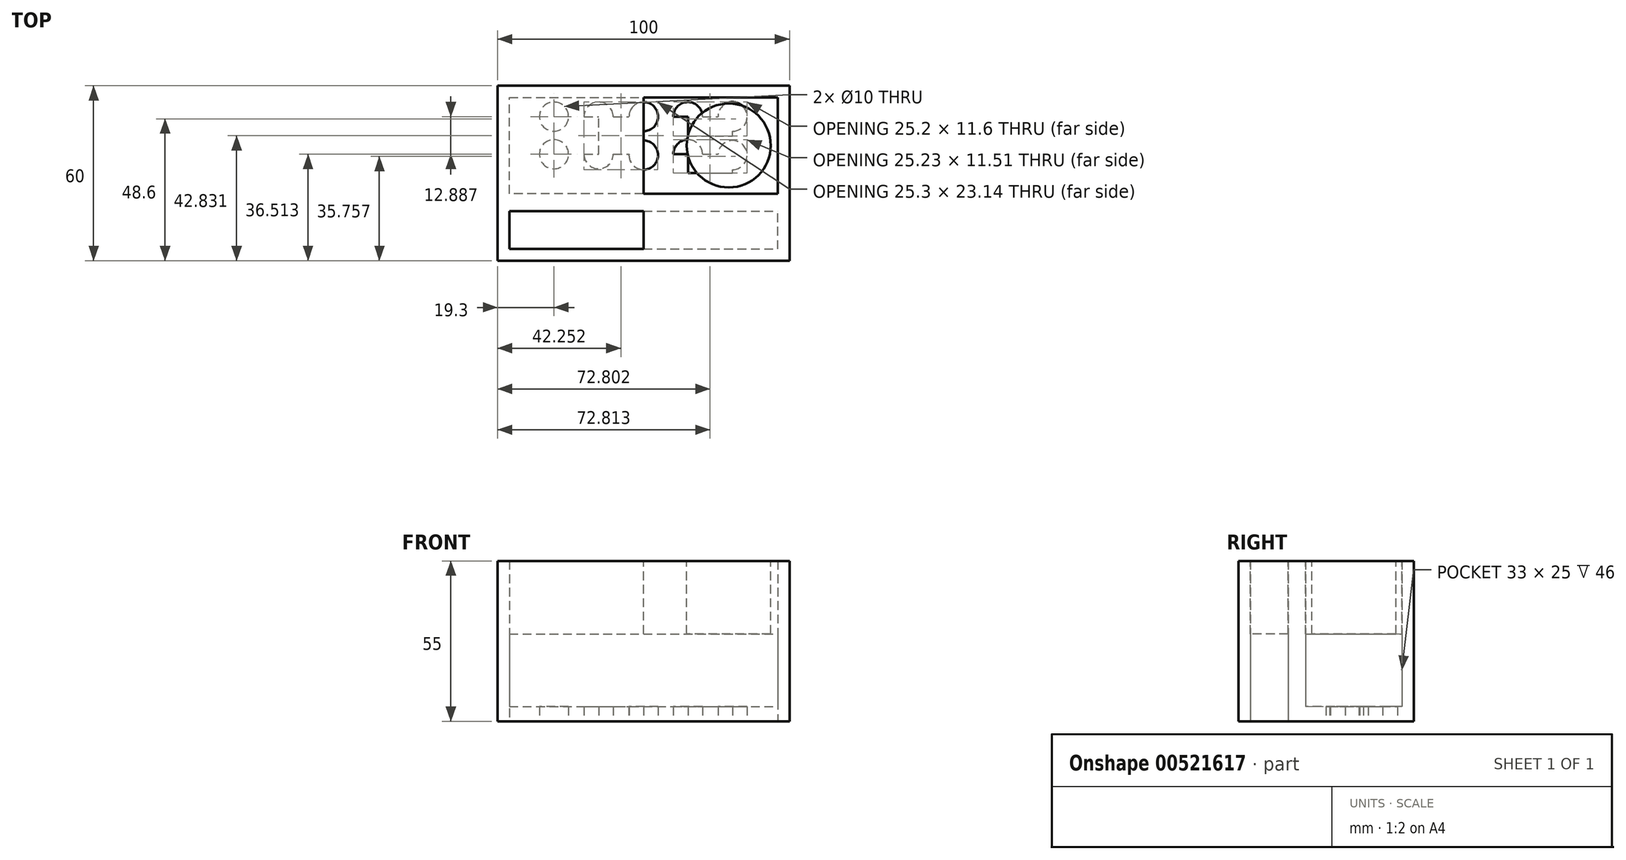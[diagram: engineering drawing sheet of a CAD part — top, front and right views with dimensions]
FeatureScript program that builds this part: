
annotation { "Feature Type Name" : "Feature", "Feature Type Description" : "" }
export const myFeature = defineFeature(function(context is Context, id is Id, definition is map)
    precondition{}
    {
        {
            var Q0;
            Q0=qCreatedBy(makeId("Top.planeOp"),FACE);
            var sketch = newSketch(context, id + "F0", { "sketchPlane" : qUnion([Q0])});
            skLineSegment(sketch, "E0.bottom", {"start": v(50, -30) * mm, "end": v(-50, -30) * mm});
            skLineSegment(sketch, "E0.top", {"start": v(50, 30) * mm, "end": v(-50, 30) * mm});
            skLineSegment(sketch, "E0.left", {"start": v(50, -30) * mm, "end": v(50, 30) * mm});
            skLineSegment(sketch, "E0.right", {"start": v(-50, -30) * mm, "end": v(-50, 30) * mm});
            skPoint(sketch, "E0.middle", {"position": v(0, 0) * mm});
            skLineSegment(sketch, "E1", {"start": v(-50, -30) * mm, "end": v(-50, -10) * mm});
            skLineSegment(sketch, "E2", {"start": v(-50, -10) * mm, "end": v(50, -10) * mm});
            skLineSegment(sketch, "E3", {"start": v(0, -10) * mm, "end": v(0, -13) * mm});
            skLineSegment(sketch, "E4", {"start": v(0, -30) * mm, "end": v(0, -26) * mm});
            skLineSegment(sketch, "E5", {"start": v(-50, 6.51) * mm, "end": v(-46, 6.51) * mm});
            skLineSegment(sketch, "E6", {"start": v(-14.58, 30) * mm, "end": v(-14.58, 26) * mm});
            skLineSegment(sketch, "E7", {"start": v(50, 11.98) * mm, "end": v(46, 11.98) * mm});
            skLineSegment(sketch, "E8", {"start": v(18.9, -10) * mm, "end": v(18.9, -7) * mm});
            skLineSegment(sketch, "E9", {"start": v(-46, -26) * mm, "end": v(46, -26) * mm});
            skLineSegment(sketch, "E10", {"start": v(46, -26) * mm, "end": v(46, -13) * mm});
            skLineSegment(sketch, "E11", {"start": v(-46, -13) * mm, "end": v(-46, -26) * mm});
            skLineSegment(sketch, "E12", {"start": v(-46, -13) * mm, "end": v(46, -13) * mm});
            skLineSegment(sketch, "E13", {"start": v(-46, -7) * mm, "end": v(-46, 26) * mm});
            skLineSegment(sketch, "E14", {"start": v(-46, 26) * mm, "end": v(46, 26) * mm});
            skLineSegment(sketch, "E15", {"start": v(46, 26) * mm, "end": v(46, -7) * mm});
            skLineSegment(sketch, "E16", {"start": v(46, -7) * mm, "end": v(-46, -7) * mm});
            skLineSegment(sketch, "E17", {"start": v(0, 26) * mm, "end": v(0, 19.4) * mm});
            skPoint(sketch, "E17.endSnap0", {"position": v(0, -7) * mm});
            skLineSegment(sketch, "E18", {"start": v(0, 19.4) * mm, "end": v(0, 12.8) * mm});
            skLineSegment(sketch, "E19", {"start": v(0, 12.8) * mm, "end": v(0, 6.2) * mm});
            skLineSegment(sketch, "E20", {"start": v(0, 6.2) * mm, "end": v(0, -0.4) * mm});
            skLineSegment(sketch, "E21", {"start": v(0, -0.4) * mm, "end": v(0, -7) * mm});
            skLineSegment(sketch, "E22", {"start": v(-46, 19.4) * mm, "end": v(46, 19.4) * mm});
            skLineSegment(sketch, "E23", {"start": v(-46, 12.8) * mm, "end": v(46, 12.8) * mm});
            skLineSegment(sketch, "E24", {"start": v(-46, 6.51) * mm, "end": v(46, 6.51) * mm});
            skLineSegment(sketch, "E25", {"start": v(-46, 0) * mm, "end": v(46, 0) * mm});
            skLineSegment(sketch, "E26", {"start": v(-46, -3.74) * mm, "end": v(-30.7, -3.74) * mm});
            skLineSegment(sketch, "E27", {"start": v(-30.7, -3.74) * mm, "end": v(-15.4, -3.74) * mm});
            skLineSegment(sketch, "E28", {"start": v(-15.4, -3.74) * mm, "end": v(-0.1, -3.74) * mm});
            skLineSegment(sketch, "E29", {"start": v(-0.1, -3.74) * mm, "end": v(15.2, -3.74) * mm});
            skLineSegment(sketch, "E30", {"start": v(15.2, -3.74) * mm, "end": v(30.5, -3.74) * mm});
            skLineSegment(sketch, "E31", {"start": v(30.5, -3.74) * mm, "end": v(46, -3.74) * mm});
            skLineSegment(sketch, "E32", {"start": v(-30.7, -7) * mm, "end": v(-30.7, 26) * mm});
            skLineSegment(sketch, "E33", {"start": v(-15.4, -7) * mm, "end": v(-15.4, 26) * mm});
            skLineSegment(sketch, "E34", {"start": v(15.2, -7) * mm, "end": v(15.2, 26) * mm});
            skLineSegment(sketch, "E35", {"start": v(30.5, -7) * mm, "end": v(30.5, 26) * mm});
            skCircle(sketch, "E36", {"center": v(-30.7, 19.4) * mm, "radius": 5 * mm});
            skCircle(sketch, "E37", {"center": v(-15.4, 19.4) * mm, "radius": 5 * mm});
            skCircle(sketch, "E38", {"center": v(0, 19.4) * mm, "radius": 5 * mm});
            skCircle(sketch, "E39", {"center": v(15.2, 19.4) * mm, "radius": 5 * mm});
            skCircle(sketch, "E40", {"center": v(30.5, 19.4) * mm, "radius": 5 * mm});
            skCircle(sketch, "E41", {"center": v(-30.7, 6.51) * mm, "radius": 5 * mm});
            skCircle(sketch, "E42", {"center": v(-15.4, 6.51) * mm, "radius": 5 * mm});
            skCircle(sketch, "E43", {"center": v(0, 6.2) * mm, "radius": 5 * mm});
            skCircle(sketch, "E44", {"center": v(15.2, 6.51) * mm, "radius": 5 * mm});
            skCircle(sketch, "E45", {"center": v(30.5, 6.2) * mm, "radius": 5 * mm});
            skSolve(sketch);
        }
        {
            var Q0;
            Q0 = qSketchRegion(id + "F0", true);
            extrude(context, id + "F1", {"entities" : qUnion([Q0]), "depth" : 30 * mm, "offsetDistance" : 25 * mm});
        }
        {
            var Q0;
            {var subQ5=sQuery(id+"F0.wireOp",EDGE,"E43");var subQ6=sQuery(id+"F0.wireOp",EDGE,"E24");var subQ7=makeQuery(id+"F0.imprint","INTERSECT",VERTEX,{"disambiguationData":[OD(1.0)],"derivedFrom":[subQ6,subQ5]});Q0=makeQuery(id+"F0.imprint","IMPRINT",FACE,{"disambiguationData":[TD([[makeQuery(id+"F0.imprint","IMPRINT",EDGE,{"disambiguationData":[TD([[subQ7,-1.0]])],"derivedFrom":subQ6}),1.0]])]});}
            var Q1;
            {var subQ5=sQuery(id+"F0.wireOp",EDGE,"E43");var subQ6=sQuery(id+"F0.wireOp",EDGE,"E20");var subQ7=makeQuery(id+"F0.imprint","INTERSECT",VERTEX,{"derivedFrom":[subQ6,subQ5]});Q1=makeQuery(id+"F0.imprint","IMPRINT",FACE,{"disambiguationData":[TD([[makeQuery(id+"F0.imprint","IMPRINT",EDGE,{"disambiguationData":[TD([[subQ7,-1.0]])],"derivedFrom":subQ6}),1.0]])]});}
            var Q2;
            {var subQ7=sQuery(id+"F0.wireOp",EDGE,"E38");var subQ8=sQuery(id+"F0.wireOp",EDGE,"E22");var subQ9=makeQuery(id+"F0.imprint","INTERSECT",VERTEX,{"disambiguationData":[OD(1.0)],"derivedFrom":[subQ8,subQ7]});Q2=makeQuery(id+"F0.imprint","IMPRINT",FACE,{"disambiguationData":[TD([[makeQuery(id+"F0.imprint","IMPRINT",EDGE,{"disambiguationData":[TD([[subQ9,-1.0]])],"derivedFrom":subQ8}),-1.0]])]});}
            var Q3;
            {var subQ1=sQuery(id+"F0.wireOp",EDGE,"E14");var subQ9=sQuery(id+"F0.wireOp",EDGE,"E17");var subQ10=makeQuery(id+"F0.imprint","INTERSECT",VERTEX,{"derivedFrom":[subQ1,subQ9]});Q3=makeQuery(id+"F0.imprint","IMPRINT",FACE,{"disambiguationData":[TD([[makeQuery(id+"F0.imprint","IMPRINT",EDGE,{"disambiguationData":[TD([[subQ10,-1.0]])],"derivedFrom":subQ1}),-1.0]])]});}
            var Q4;
            {var subQ7=sQuery(id+"F0.wireOp",EDGE,"E44");var subQ9=sQuery(id+"F0.wireOp",EDGE,"E24");var subQ10=makeQuery(id+"F0.imprint","INTERSECT",VERTEX,{"disambiguationData":[OD(1.0)],"derivedFrom":[subQ9,subQ7]});Q4=makeQuery(id+"F0.imprint","IMPRINT",FACE,{"disambiguationData":[TD([[makeQuery(id+"F0.imprint","IMPRINT",EDGE,{"disambiguationData":[TD([[subQ10,-1.0]])],"derivedFrom":subQ9}),-1.0]])]});}
            var Q5;
            {var subQ1=sQuery(id+"F0.wireOp",EDGE,"E23");var subQ5=sQuery(id+"F0.wireOp",EDGE,"E34");var subQ6=makeQuery(id+"F0.imprint","INTERSECT",VERTEX,{"derivedFrom":[subQ1,subQ5]});Q5=makeQuery(id+"F0.imprint","IMPRINT",FACE,{"disambiguationData":[TD([[makeQuery(id+"F0.imprint","IMPRINT",EDGE,{"disambiguationData":[TD([[subQ6,-1.0]])],"derivedFrom":subQ1}),-1.0]])]});}
            var Q6;
            {var subQ7=sQuery(id+"F0.wireOp",EDGE,"E22");var subQ9=sQuery(id+"F0.wireOp",EDGE,"E39");var subQ11=makeQuery(id+"F0.imprint","INTERSECT",VERTEX,{"disambiguationData":[OD(1.0)],"derivedFrom":[subQ7,subQ9]});Q6=makeQuery(id+"F0.imprint","IMPRINT",FACE,{"disambiguationData":[TD([[makeQuery(id+"F0.imprint","IMPRINT",EDGE,{"disambiguationData":[TD([[subQ11,-1.0]])],"derivedFrom":subQ7}),-1.0]])]});}
            var Q7;
            {var subQ1=sQuery(id+"F0.wireOp",EDGE,"E14");var subQ5=sQuery(id+"F0.wireOp",EDGE,"E34");var subQ6=makeQuery(id+"F0.imprint","INTERSECT",VERTEX,{"derivedFrom":[subQ1,subQ5]});Q7=makeQuery(id+"F0.imprint","IMPRINT",FACE,{"disambiguationData":[TD([[makeQuery(id+"F0.imprint","IMPRINT",EDGE,{"disambiguationData":[TD([[subQ6,-1.0]])],"derivedFrom":subQ1}),-1.0]])]});}
            var Q8;
            {var subQ1=sQuery(id+"F0.wireOp",EDGE,"E14");var subQ6=sQuery(id+"F0.wireOp",EDGE,"E15");var subQ9=makeQuery(id+"F0.imprint","INTERSECT",VERTEX,{"derivedFrom":[subQ1,subQ6]});Q8=makeQuery(id+"F0.imprint","IMPRINT",FACE,{"disambiguationData":[TD([[makeQuery(id+"F0.imprint","IMPRINT",EDGE,{"disambiguationData":[TD([[subQ9,1.0]])],"derivedFrom":subQ1}),-1.0]])]});}
            var Q9;
            {var subQ5=sQuery(id+"F0.wireOp",EDGE,"E15");var subQ7=sQuery(id+"F0.wireOp",EDGE,"E22");var subQ8=makeQuery(id+"F0.imprint","INTERSECT",VERTEX,{"derivedFrom":[subQ5,subQ7]});Q9=makeQuery(id+"F0.imprint","IMPRINT",FACE,{"disambiguationData":[TD([[makeQuery(id+"F0.imprint","IMPRINT",EDGE,{"disambiguationData":[TD([[subQ8,-1.0]])],"derivedFrom":subQ5}),-1.0]])]});}
            var Q10;
            {var subQ1=sQuery(id+"F0.wireOp",EDGE,"E15");var subQ5=makeQuery(id+"F0.imprint","INTERSECT",VERTEX,{"derivedFrom":[sQuery(id+"F0.wireOp",EDGE,"E7"),subQ1]});Q10=makeQuery(id+"F0.imprint","IMPRINT",FACE,{"disambiguationData":[TD([[makeQuery(id+"F0.imprint","IMPRINT",EDGE,{"disambiguationData":[TD([[subQ5,1.0]])],"derivedFrom":subQ1}),-1.0]])]});}
            var Q11;
            {var subQ0=sQuery(id+"F0.wireOp",EDGE,"E24");var subQ1=sQuery(id+"F0.wireOp",EDGE,"E15");var subQ2=makeQuery(id+"F0.imprint","INTERSECT",VERTEX,{"derivedFrom":[subQ1,subQ0]});Q11=makeQuery(id+"F0.imprint","IMPRINT",FACE,{"disambiguationData":[TD([[makeQuery(id+"F0.imprint","IMPRINT",EDGE,{"disambiguationData":[TD([[subQ2,-1.0]])],"derivedFrom":subQ1}),-1.0]])]});}
            var Q12;
            {var subQ1=sQuery(id+"F0.wireOp",EDGE,"E20");var subQ5=sQuery(id+"F0.wireOp",EDGE,"E43");var subQ6=makeQuery(id+"F0.imprint","INTERSECT",VERTEX,{"derivedFrom":[subQ1,subQ5]});Q12=makeQuery(id+"F0.imprint","IMPRINT",FACE,{"disambiguationData":[TD([[makeQuery(id+"F0.imprint","IMPRINT",EDGE,{"disambiguationData":[TD([[subQ6,-1.0]])],"derivedFrom":subQ1}),-1.0]])]});}
            var Q13;
            {var subQ3=sQuery(id+"F0.wireOp",EDGE,"E42");var subQ5=sQuery(id+"F0.wireOp",EDGE,"E24");var subQ6=makeQuery(id+"F0.imprint","INTERSECT",VERTEX,{"disambiguationData":[OD(1.0)],"derivedFrom":[subQ5,subQ3]});Q13=makeQuery(id+"F0.imprint","IMPRINT",FACE,{"disambiguationData":[TD([[makeQuery(id+"F0.imprint","IMPRINT",EDGE,{"disambiguationData":[TD([[subQ6,-1.0]])],"derivedFrom":subQ5}),1.0]])]});}
            var Q14;
            {var subQ3=sQuery(id+"F0.wireOp",EDGE,"E37");var subQ7=sQuery(id+"F0.wireOp",EDGE,"E22");var subQ8=makeQuery(id+"F0.imprint","INTERSECT",VERTEX,{"disambiguationData":[OD(1.0)],"derivedFrom":[subQ7,subQ3]});Q14=makeQuery(id+"F0.imprint","IMPRINT",FACE,{"disambiguationData":[TD([[makeQuery(id+"F0.imprint","IMPRINT",EDGE,{"disambiguationData":[TD([[subQ8,-1.0]])],"derivedFrom":subQ7}),-1.0]])]});}
            var Q15;
            {var subQ6=sQuery(id+"F0.wireOp",EDGE,"E14");var subQ9=makeQuery(id+"F0.imprint","INTERSECT",VERTEX,{"derivedFrom":[sQuery(id+"F0.wireOp",EDGE,"E6"),subQ6]});Q15=makeQuery(id+"F0.imprint","IMPRINT",FACE,{"disambiguationData":[TD([[makeQuery(id+"F0.imprint","IMPRINT",EDGE,{"disambiguationData":[TD([[subQ9,1.0]])],"derivedFrom":subQ6}),-1.0]])]});}
            var Q16;
            {var subQ1=sQuery(id+"F0.wireOp",EDGE,"E14");var subQ5=sQuery(id+"F0.wireOp",EDGE,"E32");var subQ6=makeQuery(id+"F0.imprint","INTERSECT",VERTEX,{"derivedFrom":[subQ1,subQ5]});Q16=makeQuery(id+"F0.imprint","IMPRINT",FACE,{"disambiguationData":[TD([[makeQuery(id+"F0.imprint","IMPRINT",EDGE,{"disambiguationData":[TD([[subQ6,-1.0]])],"derivedFrom":subQ1}),-1.0]])]});}
            var Q17;
            {var subQ1=sQuery(id+"F0.wireOp",EDGE,"E14");var subQ6=sQuery(id+"F0.wireOp",EDGE,"E13");var subQ9=makeQuery(id+"F0.imprint","INTERSECT",VERTEX,{"derivedFrom":[subQ6,subQ1]});Q17=makeQuery(id+"F0.imprint","IMPRINT",FACE,{"disambiguationData":[TD([[makeQuery(id+"F0.imprint","IMPRINT",EDGE,{"disambiguationData":[TD([[subQ9,1.0]])],"derivedFrom":subQ6}),-1.0]])]});}
            var Q18;
            {var subQ5=sQuery(id+"F0.wireOp",EDGE,"E13");var subQ7=sQuery(id+"F0.wireOp",EDGE,"E22");var subQ9=makeQuery(id+"F0.imprint","INTERSECT",VERTEX,{"derivedFrom":[subQ5,subQ7]});Q18=makeQuery(id+"F0.imprint","IMPRINT",FACE,{"disambiguationData":[TD([[makeQuery(id+"F0.imprint","IMPRINT",EDGE,{"disambiguationData":[TD([[subQ9,1.0]])],"derivedFrom":subQ5}),-1.0]])]});}
            var Q19;
            {var subQ7=sQuery(id+"F0.wireOp",EDGE,"E36");var subQ9=sQuery(id+"F0.wireOp",EDGE,"E22");var subQ10=makeQuery(id+"F0.imprint","INTERSECT",VERTEX,{"disambiguationData":[OD(1.0)],"derivedFrom":[subQ9,subQ7]});Q19=makeQuery(id+"F0.imprint","IMPRINT",FACE,{"disambiguationData":[TD([[makeQuery(id+"F0.imprint","IMPRINT",EDGE,{"disambiguationData":[TD([[subQ10,-1.0]])],"derivedFrom":subQ9}),-1.0]])]});}
            var Q20;
            {var subQ1=sQuery(id+"F0.wireOp",EDGE,"E23");var subQ5=sQuery(id+"F0.wireOp",EDGE,"E32");var subQ6=makeQuery(id+"F0.imprint","INTERSECT",VERTEX,{"derivedFrom":[subQ1,subQ5]});Q20=makeQuery(id+"F0.imprint","IMPRINT",FACE,{"disambiguationData":[TD([[makeQuery(id+"F0.imprint","IMPRINT",EDGE,{"disambiguationData":[TD([[subQ6,-1.0]])],"derivedFrom":subQ1}),-1.0]])]});}
            var Q21;
            {var subQ1=sQuery(id+"F0.wireOp",EDGE,"E13");var subQ6=sQuery(id+"F0.wireOp",EDGE,"E23");var subQ9=makeQuery(id+"F0.imprint","INTERSECT",VERTEX,{"derivedFrom":[subQ1,subQ6]});Q21=makeQuery(id+"F0.imprint","IMPRINT",FACE,{"disambiguationData":[TD([[makeQuery(id+"F0.imprint","IMPRINT",EDGE,{"disambiguationData":[TD([[subQ9,-1.0]])],"derivedFrom":subQ6}),-1.0]])]});}
            var Q22;
            {var subQ1=sQuery(id+"F0.wireOp",EDGE,"E13");var subQ6=sQuery(id+"F0.wireOp",EDGE,"E25");var subQ9=makeQuery(id+"F0.imprint","INTERSECT",VERTEX,{"derivedFrom":[subQ1,subQ6]});Q22=makeQuery(id+"F0.imprint","IMPRINT",FACE,{"disambiguationData":[TD([[makeQuery(id+"F0.imprint","IMPRINT",EDGE,{"disambiguationData":[TD([[subQ9,-1.0]])],"derivedFrom":subQ6}),1.0]])]});}
            var Q23;
            {var subQ7=sQuery(id+"F0.wireOp",EDGE,"E41");var subQ9=sQuery(id+"F0.wireOp",EDGE,"E24");var subQ10=makeQuery(id+"F0.imprint","INTERSECT",VERTEX,{"disambiguationData":[OD(1.0)],"derivedFrom":[subQ9,subQ7]});Q23=makeQuery(id+"F0.imprint","IMPRINT",FACE,{"disambiguationData":[TD([[makeQuery(id+"F0.imprint","IMPRINT",EDGE,{"disambiguationData":[TD([[subQ10,-1.0]])],"derivedFrom":subQ9}),-1.0]])]});}
            var Q24;
            {var subQ3=sQuery(id+"F0.wireOp",EDGE,"E26");Q24=makeQuery(id+"F0.imprint","IMPRINT",FACE,{"disambiguationData":[TD([[makeQuery(id+"F0.imprint","IMPRINT",EDGE,{"derivedFrom":subQ3}),1.0]])]});}
            var Q25;
            {var subQ5=sQuery(id+"F0.wireOp",EDGE,"E27");Q25=makeQuery(id+"F0.imprint","IMPRINT",FACE,{"disambiguationData":[TD([[makeQuery(id+"F0.imprint","IMPRINT",EDGE,{"derivedFrom":subQ5}),1.0]])]});}
            var Q26;
            {var subQ0=sQuery(id+"F0.wireOp",EDGE,"E28");Q26=makeQuery(id+"F0.imprint","IMPRINT",FACE,{"disambiguationData":[TD([[makeQuery(id+"F0.imprint","IMPRINT",EDGE,{"derivedFrom":subQ0}),1.0]])]});}
            var Q27;
            {var subQ1=sQuery(id+"F0.wireOp",EDGE,"E20");var subQ5=sQuery(id+"F0.wireOp",EDGE,"E21");var subQ6=makeQuery(id+"F0.imprint","INTERSECT",VERTEX,{"derivedFrom":[subQ1,subQ5]});Q27=makeQuery(id+"F0.imprint","IMPRINT",FACE,{"disambiguationData":[TD([[makeQuery(id+"F0.imprint","IMPRINT",EDGE,{"disambiguationData":[TD([[subQ6,1.0]])],"derivedFrom":subQ1}),1.0]])]});}
            var Q28;
            {var subQ5=sQuery(id+"F0.wireOp",EDGE,"E30");Q28=makeQuery(id+"F0.imprint","IMPRINT",FACE,{"disambiguationData":[TD([[makeQuery(id+"F0.imprint","IMPRINT",EDGE,{"derivedFrom":subQ5}),1.0]])]});}
            var Q29;
            {var subQ3=sQuery(id+"F0.wireOp",EDGE,"E31");Q29=makeQuery(id+"F0.imprint","IMPRINT",FACE,{"disambiguationData":[TD([[makeQuery(id+"F0.imprint","IMPRINT",EDGE,{"derivedFrom":subQ3}),1.0]])]});}
            var Q30;
            {var subQ3=sQuery(id+"F0.wireOp",EDGE,"E26");Q30=makeQuery(id+"F0.imprint","IMPRINT",FACE,{"disambiguationData":[TD([[makeQuery(id+"F0.imprint","IMPRINT",EDGE,{"derivedFrom":subQ3}),-1.0]])]});}
            var Q31;
            {var subQ5=sQuery(id+"F0.wireOp",EDGE,"E27");Q31=makeQuery(id+"F0.imprint","IMPRINT",FACE,{"disambiguationData":[TD([[makeQuery(id+"F0.imprint","IMPRINT",EDGE,{"derivedFrom":subQ5}),-1.0]])]});}
            var Q32;
            {var subQ1=sQuery(id+"F0.wireOp",EDGE,"E28");Q32=makeQuery(id+"F0.imprint","IMPRINT",FACE,{"disambiguationData":[TD([[makeQuery(id+"F0.imprint","IMPRINT",EDGE,{"derivedFrom":subQ1}),-1.0]])]});}
            var Q33;
            {var subQ0=sQuery(id+"F0.wireOp",EDGE,"E21");var subQ1=sQuery(id+"F0.wireOp",EDGE,"E16");var subQ2=makeQuery(id+"F0.imprint","INTERSECT",VERTEX,{"derivedFrom":[subQ1,subQ0]});Q33=makeQuery(id+"F0.imprint","IMPRINT",FACE,{"disambiguationData":[TD([[makeQuery(id+"F0.imprint","IMPRINT",EDGE,{"disambiguationData":[TD([[subQ2,1.0]])],"derivedFrom":subQ1}),-1.0]])]});}
            var Q34;
            {var subQ1=sQuery(id+"F0.wireOp",EDGE,"E30");Q34=makeQuery(id+"F0.imprint","IMPRINT",FACE,{"disambiguationData":[TD([[makeQuery(id+"F0.imprint","IMPRINT",EDGE,{"derivedFrom":subQ1}),-1.0]])]});}
            var Q35;
            {var subQ3=sQuery(id+"F0.wireOp",EDGE,"E31");Q35=makeQuery(id+"F0.imprint","IMPRINT",FACE,{"disambiguationData":[TD([[makeQuery(id+"F0.imprint","IMPRINT",EDGE,{"derivedFrom":subQ3}),-1.0]])]});}
            extrude(context, id + "F2", {"entities" : qUnion([Q0, Q1, Q2, Q3, Q4, Q5, Q6, Q7, Q8, Q9, Q10, Q11, Q12, Q13, Q14, Q15, Q16, Q17, Q18, Q19, Q20, Q21, Q22, Q23, Q24, Q25, Q26, Q27, Q28, Q29, Q30, Q31, Q32, Q33, Q34, Q35]), "operationType" : NewBodyOperationType.ADD, "depth" : 5 * mm, "offsetDistance" : 25 * mm});
        }
        {
            var Q0;
            Q0=makeQuery(id+"F1.opExtrude","CAP_FACE",FACE,{"disambiguationData":[OSD([sQuery(id+"F0.wireOp",EDGE,"E0.bottom"),sQuery(id+"F0.wireOp",EDGE,"E0.top"),sQuery(id+"F0.wireOp",EDGE,"E0.left"),sQuery(id+"F0.wireOp",EDGE,"E0.right"),sQuery(id+"F0.wireOp",EDGE,"E1"),sQuery(id+"F0.wireOp",EDGE,"E9"),sQuery(id+"F0.wireOp",EDGE,"E10"),sQuery(id+"F0.wireOp",EDGE,"E11"),sQuery(id+"F0.wireOp",EDGE,"E12"),sQuery(id+"F0.wireOp",EDGE,"E13"),sQuery(id+"F0.wireOp",EDGE,"E14"),sQuery(id+"F0.wireOp",EDGE,"E15"),sQuery(id+"F0.wireOp",EDGE,"E16")])],"isStart":false});
            var sketch = newSketch(context, id + "F3", { "sketchPlane" : qUnion([Q0])});
            skLineSegment(sketch, "E46", {"start": v(-50, -30) * mm, "end": v(-50, 30) * mm});
            skLineSegment(sketch, "E47", {"start": v(-50, 30) * mm, "end": v(50, 30) * mm});
            skLineSegment(sketch, "E48", {"start": v(50, 30) * mm, "end": v(50, -30) * mm});
            skLineSegment(sketch, "E49", {"start": v(50, -30) * mm, "end": v(-50, -30) * mm});
            skSolve(sketch);
        }
        {
            var Q0;
            Q0=makeQuery(id+"F3.imprint","IMPRINT",FACE,{"disambiguationData":[TD([[makeQuery(id+"F3.imprint","IMPRINT",EDGE,{"derivedFrom":makeQuery(id+"F1.opExtrude","CAP_EDGE",EDGE,{"disambiguationData":[OSD([sQuery(id+"F0.wireOp",EDGE,"E9")])],"isStart":false})}),1.0]])]});
            var Q1;
            Q1=makeQuery(id+"F3.imprint","IMPRINT",FACE,{"disambiguationData":[TD([[makeQuery(id+"F3.imprint","IMPRINT",EDGE,{"derivedFrom":makeQuery(id+"F1.opExtrude","CAP_EDGE",EDGE,{"disambiguationData":[OSD([sQuery(id+"F0.wireOp",EDGE,"E13")])],"isStart":false})}),-1.0]])]});
            var Q2;
            Q2=makeQuery(id+"F3.imprint","IMPRINT",FACE,{"disambiguationData":[TD([[makeQuery(id+"F3.imprint","IMPRINT",EDGE,{"derivedFrom":sQuery(id+"F3.wireOp",EDGE,"E46")}),-1.0]])]});
            extrude(context, id + "F4", {"entities" : qUnion([Q0, Q1, Q2]), "operationType" : NewBodyOperationType.ADD, "depth" : 25 * mm, "offsetDistance" : 25 * mm});
        }
        {
            var Q0;
            Q0=makeQuery(id+"F4.opExtrude","CAP_FACE",FACE,{"disambiguationData":[OSD([sQuery(id+"F3.wireOp",EDGE,"E46"),sQuery(id+"F3.wireOp",EDGE,"E47"),sQuery(id+"F3.wireOp",EDGE,"E48"),sQuery(id+"F3.wireOp",EDGE,"E49")])],"isStart":false});
            var sketch = newSketch(context, id + "F5", { "sketchPlane" : qUnion([Q0])});
            skLineSegment(sketch, "E50.0", {"start": v(-46, -26) * mm, "end": v(46, -26) * mm});
            skLineSegment(sketch, "E50.1", {"start": v(-46, -13) * mm, "end": v(46, -13) * mm});
            skLineSegment(sketch, "E50.2", {"start": v(46, -26) * mm, "end": v(46, -13) * mm});
            skLineSegment(sketch, "E50.3", {"start": v(-46, -13) * mm, "end": v(-46, -26) * mm});
            skLineSegment(sketch, "E51", {"start": v(0, -13) * mm, "end": v(0, -7) * mm});
            skPoint(sketch, "E51.endSnap0", {"position": v(0, -13) * mm});
            skLineSegment(sketch, "E52", {"start": v(0, 30) * mm, "end": v(0, 26) * mm});
            skLineSegment(sketch, "E53", {"start": v(50, 1.69) * mm, "end": v(46, 1.69) * mm});
            skLineSegment(sketch, "E54", {"start": v(-50, 0) * mm, "end": v(-46, 0) * mm});
            skPoint(sketch, "E54.endSnap0", {"position": v(-50, 0) * mm});
            skLineSegment(sketch, "E55", {"start": v(46, -7) * mm, "end": v(46, 26) * mm});
            skLineSegment(sketch, "E56", {"start": v(46, 26) * mm, "end": v(-46, 26) * mm});
            skLineSegment(sketch, "E57", {"start": v(-46, 26) * mm, "end": v(-46, -7) * mm});
            skLineSegment(sketch, "E58", {"start": v(-46, -7) * mm, "end": v(46, -7) * mm});
            skLineSegment(sketch, "E59", {"start": v(0, 26) * mm, "end": v(0, -7) * mm});
            skLineSegment(sketch, "E60", {"start": v(46, 9.5) * mm, "end": v(-46, 9.5) * mm});
            skLineSegment(sketch, "E61", {"start": v(46, 9.5) * mm, "end": v(29.2, 9.5) * mm});
            skLineSegment(sketch, "E62", {"start": v(29.2, 9.5) * mm, "end": v(29.2, 3.56) * mm});
            skCircle(sketch, "E63", {"center": v(29.2, 9.5) * mm, "radius": 14.4 * mm});
            skLineSegment(sketch, "E64", {"start": v(0, -13) * mm, "end": v(0, -26) * mm});
            skLineSegment(sketch, "E65", {"start": v(0, -13) * mm, "end": v(0, -10) * mm});
            skLineSegment(sketch, "E66", {"start": v(0, -10) * mm, "end": v(-46.01, -10) * mm});
            skLineSegment(sketch, "E67", {"start": v(-46.01, -10) * mm, "end": v(-46, -13) * mm});
            skSolve(sketch);
        }
        {
            var Q0;
            {var subQ0=sQuery(id+"F5.wireOp",EDGE,"E61");var subQ1=sQuery(id+"F5.wireOp",EDGE,"E60");var subQ2=makeQuery(id+"F5.imprint","INTERSECT",VERTEX,{"derivedFrom":[subQ1,subQ0]});Q0=makeQuery(id+"F5.imprint","IMPRINT",FACE,{"disambiguationData":[TD([[makeQuery(id+"F5.imprint","IMPRINT",EDGE,{"disambiguationData":[TD([[subQ2,-1.0]])],"derivedFrom":subQ1}),-1.0]])]});}
            var Q1;
            {var subQ0=sQuery(id+"F5.wireOp",EDGE,"E61");var subQ1=sQuery(id+"F5.wireOp",EDGE,"E60");var subQ2=makeQuery(id+"F5.imprint","INTERSECT",VERTEX,{"derivedFrom":[subQ1,subQ0]});Q1=makeQuery(id+"F5.imprint","IMPRINT",FACE,{"disambiguationData":[TD([[makeQuery(id+"F5.imprint","IMPRINT",EDGE,{"disambiguationData":[TD([[subQ2,-1.0]])],"derivedFrom":subQ1}),1.0]])]});}
            extrude(context, id + "F6", {"entities" : qUnion([Q0, Q1]), "operationType" : NewBodyOperationType.REMOVE, "oppositeDirection" : true, "depth" : 25 * mm, "offsetDistance" : 25 * mm});
        }
        {
            var Q0;
            {var subQ0=sQuery(id+"F5.wireOp",EDGE,"E50.3");Q0=makeQuery(id+"F5.imprint","IMPRINT",FACE,{"disambiguationData":[TD([[makeQuery(id+"F5.imprint","IMPRINT",EDGE,{"derivedFrom":subQ0}),1.0]])]});}
            var Q1;
            {var subQ2=sQuery(id+"F5.wireOp",EDGE,"E65");Q1=makeQuery(id+"F5.imprint","IMPRINT",FACE,{"disambiguationData":[TD([[makeQuery(id+"F5.imprint","IMPRINT",EDGE,{"derivedFrom":subQ2}),1.0]])]});}
            extrude(context, id + "F7", {"entities" : qUnion([Q0, Q1]), "operationType" : NewBodyOperationType.REMOVE, "oppositeDirection" : true, "depth" : 25 * mm, "offsetDistance" : 25 * mm});
        }
    });
